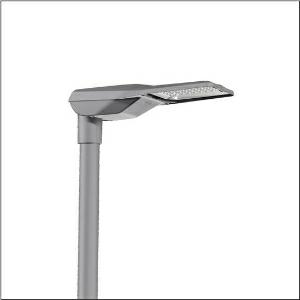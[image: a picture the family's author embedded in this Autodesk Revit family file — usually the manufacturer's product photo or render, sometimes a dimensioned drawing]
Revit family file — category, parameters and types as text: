
# Revit family: streetlight_sl_21_iq_mini___st0_8a_5xe2c31d08gb_9b37
name_source: partatom
category: Lighting Fixtures
units: mm (PartAtom-declared; Revit-internal decimal feet)

## family parameters
Cut with Voids When Loaded = No
Host = Face
Light Source = No
Part Type = Normal
Room Calculation Point = No
Round Connector Dimension = Use Diameter
Shared = No

## types (1)
- --- (1 x LED, 5680 lm, 37.1 W, 3000K)
    Apparent Load = 37 VA
    CIE Flux Codes = 38 75 97 100 100
    Color Rendering = 70
    Color Temperature = 3000K
    Default Elevation = 1800 mm
    Description = Streetlight SL 21 mini, mast luminaire, primary light control with lens, of PMMA, primary optical cover: cover, of toughened safety glass, transparent, light distribution: ST0.8a, light emission: direct distribution, primary light characteristic: asymmetric, installation type: post-top, side-entry, LED, High Power LED, rated luminous flux: 5.680lm, luminous efficacy: 153lm/W, light colour: 730, colour temperature: 3000K, control gear: ECG iQ, control: Auto-Match, Temp-Guard, Lumen-Switch, Night-Set, Smart-Wire, Light-Fading, Desk-Remote (wireless, voltage-free reading and setting of iQ features in the workshop via application-optimized NFC function/RFID function), optimised constant luminous flux control (CLO 2.0), mains connection: 220..240V, AC, 50/60Hz, start of lifetime: 37W, end of lifetime: 39W, reduction: 18W, luminaire housing, of diecast aluminium, powder-coated, Siteco® metallic grey (DB 702S), corrosivity category C5 according to DIN EN ISO 12944, length: 628mm, width: 235mm, height: 110mm, spigot size: 60/76mm (post-top) and 42/60/76mm (side-entry), mast flange for spigot size: 42mm: 5XC10008XM4, 60mm: 5XC10008XM2, 76/60mm: 5XC10108XM1, protection rating (complete): IP66, insulation class (complete): insulation class II (safety insulation), certification: CE, ENEC, VDE, impact resistance: IK09, permissible operating ambient temperature for outdoor applications: -40..+50°C, standard-compliant lighting for roads and squares, packaging unit: 1 piece

Light Distribution: ST0.8a
    Height = 110 mm
    Lamp = 1 x LED
    Lamp Light Flux = 5680 lm
    Lamp Power = 37.1 W
    Lamp count = 1
    Length = 625 mm
    Luminous efficacy = 153 lm/W
    Manufacturer = Siteco
    ModVariant = No
    Model = 5XE2C31D08GB
    Number of Poles = 1
    OnlyDefault = Yes
    Power Factor = 1
    Product Name = Streetlight SL 21 iQ mini | ST0.8a
    Product group = mast luminaire | pylon top
    ProductGroupID = 6100
    Protection Class = Protection class II
    Protection Degree = IP 66
    RLX_Detail_Level = 1
    RlxData = <blob elided: 92001 chars, md5=3d7fa252>
    Socket = socket
    Standby Power = 0 W
    System Light Flux = 5680 lm
    System Power = 37 W
    Type Comments = factory setting: luminous flux: 100 % | dim-lin: 254 | 385 mA
    Type Image = l_1003519.jpg
    URL = http://relux.com
    VarID = @adj_101961
    Voltage = 0 V
    Weight = 0.00 kg
    Width = 234 mm

## geometry (parser evidence)
native form markers: Blend x4, Sweep x11
no freeform markers — native parametric forms only
